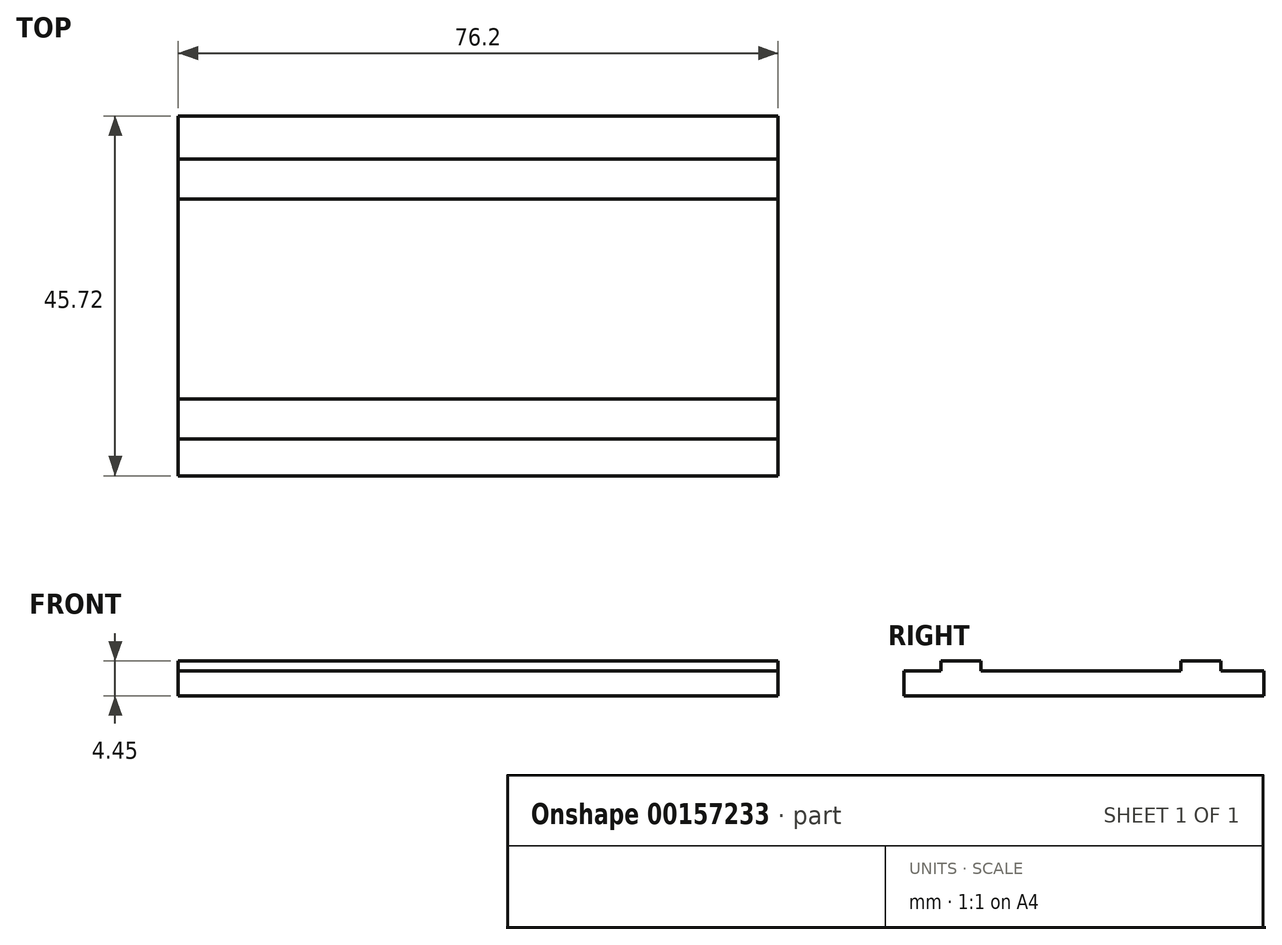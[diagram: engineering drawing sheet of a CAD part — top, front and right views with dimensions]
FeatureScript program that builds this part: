
annotation { "Feature Type Name" : "Feature", "Feature Type Description" : "" }
export const myFeature = defineFeature(function(context is Context, id is Id, definition is map)
    precondition{}
    {
        {
            var Q0;
            Q0=qCreatedBy(makeId("Top.planeOp"),FACE);
            var sketch = newSketch(context, id + "F0", { "sketchPlane" : qUnion([Q0])});
            skLineSegment(sketch, "E0", {"start": v(0, 22.86) * mm, "end": v(-76.2, 22.86) * mm});
            skLineSegment(sketch, "E1", {"start": v(-76.2, 22.86) * mm, "end": v(-76.2, 27.94) * mm});
            skLineSegment(sketch, "E2", {"start": v(-76.2, 27.94) * mm, "end": v(0, 27.94) * mm});
            skLineSegment(sketch, "E3", {"start": v(0, 27.94) * mm, "end": v(0, 22.86) * mm});
            skLineSegment(sketch, "E4", {"start": v(-66.04, -35.56) * mm, "end": v(-60.96, -35.56) * mm});
            skLineSegment(sketch, "E5", {"start": v(-76.2, -17.78) * mm, "end": v(0, -17.78) * mm});
            skLineSegment(sketch, "E6", {"start": v(-76.2, -17.78) * mm, "end": v(-76.2, 22.86) * mm});
            skLineSegment(sketch, "E7", {"start": v(-76.2, -12.7) * mm, "end": v(0, -12.7) * mm});
            skLineSegment(sketch, "E8", {"start": v(-76.2, 22.86) * mm, "end": v(-76.2, 22.86) * mm});
            skLineSegment(sketch, "E9", {"start": v(0, -12.7) * mm, "end": v(0, -17.78) * mm});
            skLineSegment(sketch, "E10", {"start": v(0, 22.86) * mm, "end": v(0, -12.7) * mm});
            skSolve(sketch);
        }
        {
            var Q0;
            Q0 = qSketchRegion(id + "F0", true);
            extrude(context, id + "F1", {"entities" : qUnion([Q0]), "depth" : 3.17 * mm});
        }
        {
            var Q0;
            Q0=makeQuery(id+"F1.opExtrude","CAP_FACE",FACE,{"disambiguationData":[OSD([sQuery(id+"F0.wireOp",EDGE,"QrAQiVZ5-jjWT-CZs4-s3iZ-MM4wZzOkzx47"),sQuery(id+"F0.wireOp",EDGE,"E1"),sQuery(id+"F0.wireOp",EDGE,"E3"),sQuery(id+"F0.wireOp",EDGE,"YqAGT16m-AJja-1JLS-Oqt2-5bfETo2h65PI"),sQuery(id+"F0.wireOp",EDGE,"c9NXRoBb-k0K7-QQuy-1dwV-VbfSVeU31zwy"),sQuery(id+"F0.wireOp",EDGE,"H2ZjSbN3-yxFl-JJjZ-YiOV-AGiw76LRMQaL"),sQuery(id+"F0.wireOp",EDGE,"M2VVD6xz-8bxF-wnww-x7FG-6UXF4FOdaWDe"),sQuery(id+"F0.wireOp",EDGE,"dZigh0te-IhLf-40TI-2o7o-2E2Ufqenbo21"),sQuery(id+"F0.wireOp",EDGE,"azlanKPs-Wgcj-TtKR-slZh-QqPIDbgpIs9C"),sQuery(id+"F0.wireOp",EDGE,"8RpLOHW4-sz7w-Mfa2-8eKL-MQAbqNgU9cph"),sQuery(id+"F0.wireOp",EDGE,"Tj6fk3vq-UMNL-AMEn-I7v9-Cscb9Hse1dhW"),sQuery(id+"F0.wireOp",EDGE,"RqmzUraB-bp07-cxGd-9ATQ-F9oE20ErbRrn"),sQuery(id+"F0.wireOp",EDGE,"VJU3m5xJ-u2t7-l5nU-WBru-DnM55yEZB2Ay"),sQuery(id+"F0.wireOp",EDGE,"fNtdLoH8-iHTW-1FXP-iZ7y-CQIlbTQ0GEB7"),sQuery(id+"F0.wireOp",EDGE,"q4WqxrF9-wKbY-u7QG-WwJF-W8UhlOC8nMXJ"),sQuery(id+"F0.wireOp",EDGE,"6UQaaGDr-X80X-vuLr-c0K2-tvEZiPN0iExL"),sQuery(id+"F0.wireOp",EDGE,"2hHopks7-iIYe-TqED-PKPY-ox780PIY7Su4"),sQuery(id+"F0.wireOp",EDGE,"4h8aECD9-UnDV-7LwE-5I3q-IAcII3rG7hb3"),sQuery(id+"F0.wireOp",EDGE,"OzX1sdCR-40ZK-aTio-xI2s-IxGSyCDaBa23"),sQuery(id+"F0.wireOp",EDGE,"S1tFx6rF-6nMB-miHy-vlSY-bkZ7Q3WquVto"),sQuery(id+"F0.wireOp",EDGE,"54DTfxFK-RXRH-IJ0y-s8ss-q65ZKBfR2og6"),sQuery(id+"F0.wireOp",EDGE,"MnYEEPqi-wif7-Cu6x-vK7K-ZaNf26LmmoCb"),sQuery(id+"F0.wireOp",EDGE,"ZWLIb2qH-Px8h-BG84-WpO2-dQHMLo97YmGD"),sQuery(id+"F0.wireOp",EDGE,"Z3a0HnE7-U48N-fqdR-B4K0-3st4nzTld1AO"),sQuery(id+"F0.wireOp",EDGE,"LoqrqzMC-KjEY-8bSt-tGOO-aK944q3rvBjD"),sQuery(id+"F0.wireOp",EDGE,"q79a6Fmz-Xz5V-f71d-BDVn-aKfQdEOmw9kR"),sQuery(id+"F0.wireOp",EDGE,"Vxc7hlvR-VESY-FoJ4-Xyji-R9prLiaEWoTO"),sQuery(id+"F0.wireOp",EDGE,"CeC5wjCu-XK3m-pksU-SiY4-vTi7ybmMYM4W"),sQuery(id+"F0.wireOp",EDGE,"5Up0F5rm-q0v7-0ei8-FxSq-cp0ieOZZM74p"),sQuery(id+"F0.wireOp",EDGE,"txclm7YS-x3yN-bQx9-g4rS-caKQQ7m3fL8r"),sQuery(id+"F0.wireOp",EDGE,"6fBwpFyQ-2lMK-kBUk-Q2jI-ZyDF6YhqFuK6"),sQuery(id+"F0.wireOp",EDGE,"lUdJ8etY-DtlW-oKDn-v5Em-XveNEUujm0k6"),sQuery(id+"F0.wireOp",EDGE,"Ky3geyxI-Le3w-82CC-s1Or-dNJhD67bMHWh"),sQuery(id+"F0.wireOp",EDGE,"5V8rJiS2-XzZn-y3p4-TFd7-ZU3XST0jbBtH"),sQuery(id+"F0.wireOp",EDGE,"oUtdVBpm-lAm5-KD0J-G13T-Z2FOd7Jj5gJX"),sQuery(id+"F0.wireOp",EDGE,"l8dDvvVJ-gVAK-VITl-S8xY-8eOxRmDhLjX0"),sQuery(id+"F0.wireOp",EDGE,"WAgxHg1Z-TKdn-CwtB-RP4P-med7EszUp0C4"),sQuery(id+"F0.wireOp",EDGE,"pE6Ng46G-7DuN-Covx-5f3I-9QGiLCUuelnf"),sQuery(id+"F0.wireOp",EDGE,"R1dXu11T-Bcy8-f1ve-Moig-4dK23BILqw1l"),sQuery(id+"F0.wireOp",EDGE,"E4"),sQuery(id+"F0.wireOp",EDGE,"TSAxDkw5-OINq-keDr-2G7G-KLzqJkkA8uWI"),sQuery(id+"F0.wireOp",EDGE,"2WB4NzLf-I6Ll-sn5Q-L3vF-kEeuKwqXfVet"),sQuery(id+"F0.wireOp",EDGE,"N3OJT30a-lqNW-ceHO-XZkO-oom74qOro2CW"),sQuery(id+"F0.wireOp",EDGE,"MkSgWXt6-9RsA-DwL8-7nVX-P9DBxprKAFPo"),sQuery(id+"F0.wireOp",EDGE,"QCEhNXOk-7l4l-ppoE-m9a1-Tnp5xpij2W0V"),sQuery(id+"F0.wireOp",EDGE,"kphqLD89-hma7-M69X-6R1D-XfPbWe82uF6N"),sQuery(id+"F0.wireOp",EDGE,"U7myCdUC-xBg5-3wM4-Djv1-1zmNNmuhIQd7"),sQuery(id+"F0.wireOp",EDGE,"ufcDEQdQ-KXdx-cOV2-orM7-LCIzMoBWA2UA"),sQuery(id+"F0.wireOp",EDGE,"Rt3CNzwC-TnuY-7VRI-kB6n-WlxbfGKxujUI"),sQuery(id+"F0.wireOp",EDGE,"oHta8Lue-26YI-2IrY-xdhT-mfY4RdViUhOM"),sQuery(id+"F0.wireOp",EDGE,"HZDZj72X-iTNY-eAKA-f3gM-sn3QQTXnO4fk"),sQuery(id+"F0.wireOp",EDGE,"ayT7KEdK-nseS-gRyz-qSzz-pBbLlnKpOHJg"),sQuery(id+"F0.wireOp",EDGE,"RKqt2fSq-zOOy-fHTW-90Wc-nBwrboEg7tUf"),sQuery(id+"F0.wireOp",EDGE,"VhTuz9IP-BZVu-RNaP-fOhd-O00NUx7jImgi"),sQuery(id+"F0.wireOp",EDGE,"l2sgoMLh-MHNq-Scuu-0Otj-ZEJrqwzUJAtm"),sQuery(id+"F0.wireOp",EDGE,"NQk1MbxV-wU7z-XcuS-2amj-tB3EHzz8uEay"),sQuery(id+"F0.wireOp",EDGE,"Q7le4tBg-LhMk-uWLU-yigj-2gQ6X8xECt6S"),sQuery(id+"F0.wireOp",EDGE,"7VVEwCWd-Hp8I-ayfR-VOjC-K76FrH4eYKrR"),sQuery(id+"F0.wireOp",EDGE,"9laWrRt7-8Lf2-sWRJ-TlaZ-imQnx1ttTfaa"),sQuery(id+"F0.wireOp",EDGE,"FItvyCqE-oEHH-dbqw-j41D-jxM0uR3qtnBr"),sQuery(id+"F0.wireOp",EDGE,"4fAtdOpA-BrBA-tQbu-aeDT-pryjkPIxj7cT"),sQuery(id+"F0.wireOp",EDGE,"R4c8hAgD-tnc6-7d9h-UvO7-bqIPrmcEhtmj"),sQuery(id+"F0.wireOp",EDGE,"p7cSwxDm-qGox-Anwt-Y2Hk-sW9XFe4m4IIi"),sQuery(id+"F0.wireOp",EDGE,"dxQVAqoP-QmgK-6O1F-XKce-xKAvLBOq8dYw"),sQuery(id+"F0.wireOp",EDGE,"zJ3jOUDP-rB3T-PuKC-VjfO-vpqqpO0HiLB9"),sQuery(id+"F0.wireOp",EDGE,"E6"),sQuery(id+"F0.wireOp",EDGE,"t8INE7z1-VbGV-PR0Z-oOOi-SivoSkunqyEH"),sQuery(id+"F0.wireOp",EDGE,"pwq1R0j9-eKtQ-wLU9-qer1-axxbKUzqroDT"),sQuery(id+"F0.wireOp",EDGE,"QSXUMklk-N06f-HMpC-tPog-j1GTMFszdDpT"),sQuery(id+"F0.wireOp",EDGE,"Xs2YVjjr-5WVG-KMro-NoYu-yoFdc5VKvXK6"),sQuery(id+"F0.wireOp",EDGE,"5fk7MOMd-CCV5-pz47-Loa6-bC6dK4HHX6jp"),sQuery(id+"F0.wireOp",EDGE,"yyuPL6oY-ZHN9-mRy8-wRdb-Y0n4BWFtapRU"),sQuery(id+"F0.wireOp",EDGE,"FpbVRiu2-El9S-CJAD-QGZJ-QsvJ51GXTIsE"),sQuery(id+"F0.wireOp",EDGE,"Dw7Ktm5w-IVbb-rN3E-AcY9-20ajeJ45FtXV"),sQuery(id+"F0.wireOp",EDGE,"zBxekj3a-Y58e-08ev-JrRY-NVTtM0GLhCcS"),sQuery(id+"F0.wireOp",EDGE,"VKbvIL0Q-Q457-CDyZ-A4qE-hZUR5X8MFERB"),sQuery(id+"F0.wireOp",EDGE,"B0TSIitU-U9aH-vBak-n2h9-9Joc2K4kKk7w")])],"isStart":false});
            var sketch = newSketch(context, id + "F2", { "sketchPlane" : qUnion([Q0])});
            skLineSegment(sketch, "E11", {"start": v(-76.2, 22.45) * mm, "end": v(0, 22.45) * mm});
            skLineSegment(sketch, "E12", {"start": v(-76.2, 17.37) * mm, "end": v(0, 17.37) * mm});
            skLineSegment(sketch, "E13", {"start": v(0, -13.1) * mm, "end": v(-76.2, -13.1) * mm});
            skLineSegment(sketch, "E14", {"start": v(-76.2, -8.03) * mm, "end": v(0, -8.03) * mm});
            skSolve(sketch);
        }
        {
            var Q0;
            {var subQ0=sQuery(id+"F2.wireOp",EDGE,"E11");Q0=makeQuery(id+"F2.imprint","IMPRINT",FACE,{"disambiguationData":[TD([[makeQuery(id+"F2.imprint","IMPRINT",EDGE,{"derivedFrom":subQ0}),-1.0]])]});}
            var Q1;
            {var subQ0=sQuery(id+"F2.wireOp",EDGE,"E13");Q1=makeQuery(id+"F2.imprint","IMPRINT",FACE,{"disambiguationData":[TD([[makeQuery(id+"F2.imprint","IMPRINT",EDGE,{"derivedFrom":subQ0}),-1.0]])]});}
            extrude(context, id + "F3", {"entities" : qUnion([Q0, Q1]), "operationType" : NewBodyOperationType.ADD, "depth" : 1.27 * mm});
        }
    });
